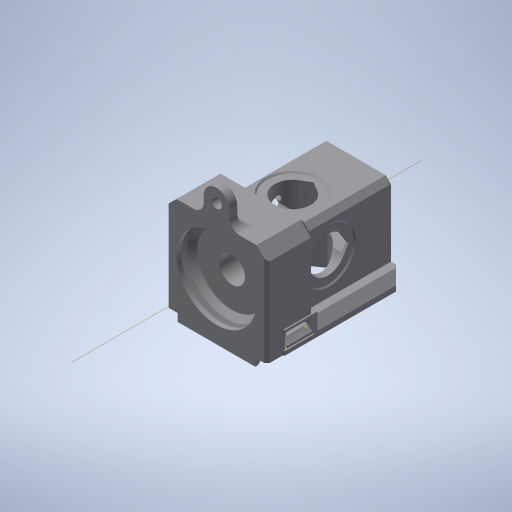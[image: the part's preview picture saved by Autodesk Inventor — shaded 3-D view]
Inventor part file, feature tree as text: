
AUTODESK INVENTOR PART (.ipt)
format: ipt  version: 2023.3 (Build 273359000, 359)  size: 1,153,024 bytes
history: native  units: mm
features: sketch x39, extrude x25, chamfer x19, hole x17, plane x17, other x10, projected_geometry x9, fillet x5, reference x3, pattern_circular x2, emboss x1, revolve x1, thicken_offset x1
ambient origin geometry x8: Origin, YZ Plane, XZ Plane, XY Plane, X Axis, Y Axis, Z Axis, Center Point
bodies: Volumenkörper1 (feature_tree)
feature tree (149):
  extrude  "Extrusion1"  Depth=40.0mm
  extrude  "Extrusion2"  Depth=47.5mm TaperAngle=0.0deg
  extrude  "Extrusion3"  Depth=23.0mm
  extrude  "Extrusion4"  Depth=20.594885mm
  sketch  "Skizze2"  dims[d2=36.0mm d3=47.5mm d4=0.0mm]
  sketch  "Skizze3"  dims[d5=23.5mm d6=23.0mm]
  hole  "Bohrung1"  [1 undecoded]
  hole  "Bohrung9"  [1 undecoded]
  extrude  "Extrusion19"  Depth=28.0mm
  hole  "Bohrung2"  [1 undecoded]
  hole  "Bohrung3"  [1 undecoded]
  sketch  "Skizze4"  dims[d7=22.0mm d8=6.0mm d9=4.0mm d10=2.0mm d11=90.0deg d12=44.5mm d13=20.594885mm]
  hole  "Bohrung4"  [1 undecoded]
  hole  "Bohrung5"  [1 undecoded]
  hole  "Bohrung6"  [1 undecoded]
  hole  "Bohrung7"  [1 undecoded]
  hole  "Bohrung8"  [1 undecoded]
  hole  "Bohrung12"  [1 undecoded]
  hole  "Bohrung13"  [1 undecoded]
  hole  "Bohrung14"  [1 undecoded]
  chamfer  "Fase1"  Distance=4.5mm
  chamfer  "Fase2"  Distance=3.0mm
  chamfer  "Fase3"  Distance=4.0mm Angle=45.0deg
  chamfer  "Fase4"  Distance=4.0mm Angle=45.0deg
  chamfer  "Fase5"  Distance=2.0mm Angle=45.0deg
  chamfer  "Fase6"  Distance=3.04mm
  chamfer  "Fase7"  Distance=4.0mm
  chamfer  "Fase8"  Distance=21.0mm
  hole  "Bohrung15"  [1 undecoded]
  extrude  "Extrusion5"  Depth=0.5mm
  extrude  "Extrusion6"  [1 undecoded]
  plane  "Arbeitsebene2"
  plane  "Arbeitsebene4"
  hole  "Bohrung17"  [1 undecoded]
  plane  "Work Plane6"
  plane  "Work Plane5"
  extrude  "Extrusion9"  [1 undecoded]
  plane  "Work Plane10"
  plane  "Work Plane8"
  sketch  "Skizze16"  dims[d62=10.0mm d63=10.0mm d64=14.0mm d65=5.0mm d66=4.0mm d67=2.0mm d68=90.0deg d69=6.0mm d70=0.0mm d71=4.0mm d72=2.0mm d73=45.0deg]
  extrude  "Extrusion7"  Depth=0.5mm
  extrude  "Extrusion10"  Depth=0.5mm TaperAngle=0.0deg
  chamfer  "Chamfer10"  Distance=20.0mm
  emboss  "Emboss1"
  extrude  "Extrusion12"  Depth=0.5mm
  fillet  "Fillet2"  [1 undecoded]
  plane  "Work Plane11"
  plane  "Work Plane16"
  extrude  "Extrusion24"  Depth=0.5mm
  extrude  "Extrusion13"  Depth=7.0mm
  fillet  "Fillet3"  Radius=31.0mm
  fillet  "Rundung1"  Radius=3.0mm
  chamfer  "Chamfer18"  Distance=4.5mm
  revolve  "Revolution1"  [1 undecoded]
  chamfer  "Chamfer11"  Distance=19.0mm
  plane  "Work Plane12"
  extrude  "Extrusion14"  Depth=0.5mm
  chamfer  "Chamfer12"  [1 undecoded]
  chamfer  "Chamfer13"  [1 undecoded]
  chamfer  "Chamfer14"  Distance=40.0mm
  chamfer  "Chamfer15"  Angle=360.0deg  [1 undecoded]
  chamfer  "Chamfer16"  Distance=2.0mm Angle=45.0deg
  plane  "Work Plane13"
  plane  "Work Plane14"
  sketch  "Sketch29"  dims[d126=23.0mm]
  hole  "Hole19"  [1 undecoded]
  extrude  "Extrusion15"  Depth=0.5mm TaperAngle=0.0deg
  fillet  "Fillet4"  Radius=6.0mm
  fillet  "Fillet5"  Radius=2.0mm
  extrude  "Extrusion16"  [1 undecoded]
  chamfer  "Chamfer19"  Distance=1.0mm
  chamfer  "Chamfer20"  Distance=5.5mm
  extrude  "Extrusion17"  Depth=0.5mm TaperAngle=0.0deg
  pattern_circular  "Circular Pattern1"  [2 undecoded]
  extrude  "Extrusion18"  TaperAngle=0.0deg  [1 undecoded]
  hole  "Hole20"  [1 undecoded]
  plane  "Work Plane15"
  extrude  "Extrusion20"  Depth=0.5mm
  plane  "Work Plane18"
  extrude  "Extrusion26"  Depth=0.5mm
  sketch  "Sketch43"  dims[d151=27.4mm d152=3.0mm d153=0.0mm d154=4.0mm d155=2.0mm d156=45.0deg d157=4.0mm d158=2.0mm d159=45.0deg d160=2.0mm d161=2.0mm d162=45.0deg]
  plane  "Work Plane17"
  extrude  "Extrusion25"  Depth=0.5mm
  hole  "Hole21"  [1 undecoded]
  extrude  "bust_through_layer_for_printing"  Depth=1.5mm
  extrude  "Extrusion23"  Depth=1.5mm
  pattern_circular  "Circular Pattern2"  [2 undecoded]
  chamfer  "Chamfer22"  Distance=3.0mm Angle=45.0deg
  thicken_offset  "Thicken1"
  extrude  "Extrusion27"  Depth=0.5mm
  sketch  "Skizze1"  dims[d0=20.0mm d1=40.0mm]
  sketch  "Skizze5"  dims[d14=22.0mm d15=6.0mm d16=4.0mm d17=2.0mm d18=90.0deg d19=21.0mm d20=0.0mm]
  sketch  "Skizze6"  dims[d242=10.0mm d243=10.0mm d23=35.5mm d24=8.2mm d25=4.0mm d26=2.0mm d27=90.0deg d28=1.2mm d29=0.0mm d30=23.5mm]
  sketch  "Skizze7"  dims[d31=23.0mm]
  sketch  "Skizze8"  dims[d32=14.0mm d33=5.0mm d34=4.0mm d35=2.0mm d36=90.0deg d37=6.0mm d38=0.0mm]
  sketch  "Skizze10"  dims[d39=14.0mm d40=5.0mm d41=4.0mm d42=2.0mm d43=90.0deg d44=6.0mm d45=0.0mm]
  sketch  "Skizze12"  dims[d240=10.0mm d241=10.0mm d48=14.0mm d49=5.0mm d50=4.0mm d51=2.0mm d52=90.0deg d53=0.5mm d54=0.0mm d56=6.0mm]
  sketch  "Skizze13"  dims[d57=28.0mm d58=28.0mm]
  plane  "Arbeitsebene3"
  other  "Arbeitsachse1"
  sketch  "Skizze15"  dims[d59=28.0mm d60=50.0mm d61=0.0mm]
  sketch  "Sketch18"  dims[d74=0.5mm d75=2.0mm d76=45.0deg d77=3.0mm d78=2.0mm d79=45.0deg]
  other  "Work Axis2"
  plane  "Work Plane7"
  projected_geometry  "Projected Loop1"
  other  "Work Axis3"
  plane  "Work Plane9"
  other  "Work Axis4"
  sketch  "Sketch19"  dims[d82=23.5mm d83=28.0mm]
  sketch  "Sketch20"  dims[d84=32.0mm d85=10.0mm d86=0.0mm]
  sketch  "Sketch21"  dims[d87=20.0mm d88=20.0mm]
  sketch  "Sketch22"  dims[d89=2.013mm d90=3.0mm d91=4.0mm d92=2.0mm d93=90.0deg d94=3.0mm d95=0.0mm d96=2.0mm d97=2.0mm d98=45.0deg]
  projected_geometry  "Projected Loop5"
  sketch  "Sketch23"  dims[d101=25.0mm d102=8.5mm d103=4.0mm d104=2.0mm d105=90.0deg d106=45.5mm d107=0.0mm]
  sketch  "Sketch24"  dims[d108=39.0mm d109=38.0mm]
  sketch  "Sketch25"  dims[d110=13.0mm d111=0.0mm d112=3.0mm d113=2.0mm d114=45.0deg]
  sketch  "Sketch26"  dims[d124=4.0mm]
  reference  "Reference2"
  reference  "Reference3"
  other  "Work Axis5"
  sketch  "Sketch28"  dims[d125=16.0mm]
  projected_geometry  "Projected Loop9"
  projected_geometry  "Projected Loop11"
  sketch  "Sketch30"  dims[d127=13.2mm d128=4.5mm d129=0.0mm]
  sketch  "Sketch31"  dims[d130=13.2mm]
  reference  "Reference5"
  sketch  "Sketch32"  dims[d131=13.2mm]
  sketch  "Sketch33"  dims[d132=13.2mm]
  sketch  "Sketch34"  dims[d133=16.0mm]
  sketch  "Sketch35"  dims[d134=4.0mm]
  sketch  "Sketch36"  dims[d135=4.0mm]
  projected_geometry  "Projected Loop13"
  projected_geometry  "Projected Loop15"
  projected_geometry  "Projected Loop17"
  sketch  "Sketch38"  dims[d137=16.0mm]
  projected_geometry  "Projected Loop19"
  sketch  "Sketch39"  dims[d138=4.0mm]
  sketch  "Sketch40"  dims[d148=25.4mm]
  sketch  "Sketch41"  dims[d149=25.4mm]
  sketch  "Sketch42"  dims[d150=27.4mm]
  sketch  "Sketch44"  dims[d190=10.0mm d191=10.0mm d165=19.9mm d166=6.0mm d167=4.0mm d168=2.0mm d169=90.0deg d170=0.5mm d171=0.0mm d172=10.0mm d173=10.0mm d174=19.9mm d175=6.0mm d176=4.0mm d177=2.0mm d178=90.0deg d179=0.5mm d180=0.0mm d181=10.0mm d182=10.0mm d183=19.9mm d184=6.0mm d185=4.0mm d186=2.0mm d187=90.0deg d188=0.5mm d189=0.0mm d192=3.04mm d193=4.0mm d194=21.0mm d195=4.134mm d196=7.0mm d197=4.0mm d198=2.0mm d199=90.0deg d200=8.0mm d201=0.0mm d203=2.5mm d204=3.5mm d217=-23.0mm d218=46.0mm d219=-7.853982mm d220=3.0mm d221=3.0mm d222=7.0mm d223=4.0mm d224=2.0mm d225=90.0deg d226=16.0mm d227=0.0mm d229=15.5mm d230=0.0mm d254=20.0mm d255=0.0mm d256=3.0mm d261=-5.235988mm d262=2.5mm d263=7.0mm d264=75.0deg d265=31.0mm d267=3.0mm d269=4.5mm d270=9.5mm d271=0.0mm d278=19.0mm d280=18.0mm d281=-3.839724mm d282=-7.853982mm d283=40.0mm d293=360.0deg d294=2.0mm d295=2.0mm d296=45.0deg d297=0.3mm d298=0.0mm d299=6.0mm d300=0.0mm d301=6.0mm d302=0.0mm d303=2.0mm d305=-6.0mm d306=1.0mm d308=5.5mm d311=10.5mm d312=0.0mm d316=9.5mm d321=0.0mm d322=31.0mm d323=2.171252mm d324=0.845184mm d325=2.0mm d327=1.5mm d328=1.5mm d329=1.5mm d330=1.5mm d331=3.0mm d332=2.0mm d333=45.0deg d334=1.0mm d335=2.5mm d336=0.5mm d337=0.0mm d340=1.5mm d341=3.5mm d342=3.5mm d343=0.0mm d344=1.0mm d345=2.0mm d346=45.0deg d347=1.0mm d348=2.0mm d349=30.0deg d350=1.0mm d351=2.0mm d352=30.0deg d353=1.0mm d354=2.0mm d355=30.0deg d356=22.0mm d357=135.0deg d358=1.2mm d359=6.0mm d360=3.0mm d361=2.0mm d362=30.0deg d366=3.15mm d367=6.0mm d368=5.0mm d369=14.0mm d370=90.0deg d371=35.0mm d372=20.594885mm d375=15.0mm d376=10.0mm d378=2.0mm d379=4.610594mm d380=0.7mm d381=2.0mm d382=45.0deg d383=6.5mm d384=10.0mm d385=4.1mm d386=3.0mm d387=0.0mm d388=4.0mm d389=3.0mm d390=30.0mm d391=4.0mm d392=0.0mm d393=3.0mm d394=2.0mm d395=45.0deg d396=3.0mm d397=11.5mm d398=45.0deg d399=0.5mm d400=2.0mm d401=45.0deg d402=1.2mm d403=1.0mm d404=0.0mm d405=30.0mm d406=180.0deg d408=9.765513mm d410=12.5mm d411=0.0mm d412=35.0mm d413=0.0mm d414=10.0mm d415=6.0mm d416=4.0mm d417=2.0mm d418=90.0deg d419=8.0mm d420=20.594885mm d421=-1.0mm d422=1.0mm d423=10.5mm d424=0.0mm d425=13.2mm d426=2.0mm d427=6.0mm d428=4.0mm d429=2.0mm d430=90.0deg d431=35.0mm d432=20.594885mm d433=11.0mm d434=19.198622mm d436=0.0mm d437=16.0mm d438=4.0mm d439=0.1mm d440=0.0mm d441=120.0deg d442=10.0mm d443=0.0mm d444=30.0mm d445=-31.415927mm d447=-7.0mm d451=2.0mm d452=2.0mm d453=45.0deg d456=9.0mm d457=0.0mm d458=0.5mm d459=1.0mm d460=3.0mm d461=8.5mm d462=0.0mm d463=8.0mm d464=0.0mm d465=2.5mm d473=0.5mm d474=0.0mm d476=1.0mm d477=0.5mm d478=0.5mm d80=1.0mm d81=1.0mm d115=1.0mm d116=1.0mm d117=1.0mm d118=1.0mm d206=1.0mm d207=1.0mm d228=1.0mm d258=1.0mm d284=1.0mm d285=1.0mm d286=0.15mm d287=0.25mm d288=0.375mm d289=14.3117mm d290=0.75mm d291=20.594885mm d292=0.0625mm d304=0.75mm d307=0.5mm d317=0.5mm d318=0.872665mm d319=0.5mm d320=0.872665mm d326=0.872665mm d338=0.0mm d339=0.0mm d374=1.0mm d377=0.15mm d409=1.0mm d435=0.0625mm d448=0.872665mm d449=0.5mm d450=0.872665mm d454=0.872665mm d466=0.872665mm d467=0.872665mm d468=0.5mm d469=0.872665mm]
  projected_geometry  "Projected Loop20"
  parser-record x1  (decoder bookkeeping rows leaked as tree rows — omitted from the tree; the rows remain in map.json)
  other  "chamber_assembly_3Dprint_bee.iam"
  other  "rod_seal_friction:1"
  other  "Sealingring_holder:1"
  other  "chamber bottom seal plate:1"
  sketch  "Sketch37"  dims[d136=16.0mm]
  extrude  "Extrusion21"  Depth=0.5mm
note: 30 required parameter values undecoded (feature->parameter linkage not recoverable at this tier; creation-order binding heuristic only, values carry confidence <= 0.55)
note: 1 file-system path scrubbed to <path> (originals preserved in map.json)